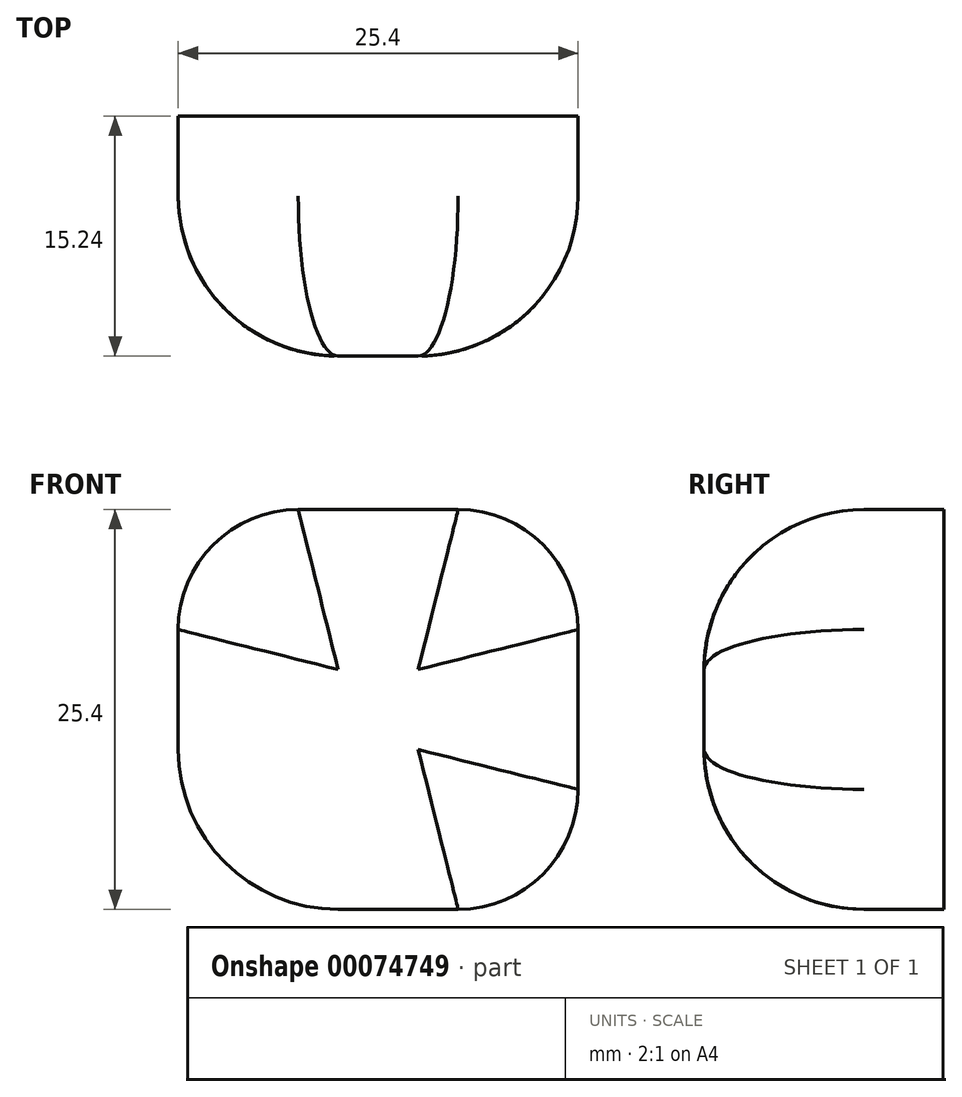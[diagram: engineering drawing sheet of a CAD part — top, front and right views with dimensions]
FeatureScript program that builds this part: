
annotation { "Feature Type Name" : "Feature", "Feature Type Description" : "" }
export const myFeature = defineFeature(function(context is Context, id is Id, definition is map)
    precondition{}
    {
        {
            var Q0;
            Q0=qCreatedBy(makeId("Front.planeOp"),FACE);
            var sketch = newSketch(context, id + "F0", { "sketchPlane" : qUnion([Q0])});
            skLineSegment(sketch, "E0", {"start": v(0, 0) * mm, "end": v(25.4, 0) * mm});
            skLineSegment(sketch, "E1", {"start": v(25.4, 0) * mm, "end": v(25.4, -25.4) * mm});
            skLineSegment(sketch, "E2", {"start": v(0, 0) * mm, "end": v(0, -25.4) * mm});
            skLineSegment(sketch, "E3", {"start": v(0, -25.4) * mm, "end": v(25.4, -25.4) * mm});
            skSolve(sketch);
        }
        {
            var Q0;
            Q0 = qSketchRegion(id + "F0", true);
            extrude(context, id + "F1", {"entities" : qUnion([Q0]), "depth" : 15.24 * mm});
        }
        {
            var Q0;
            Q0=makeQuery(id+"F1.opExtrude","SWEPT_EDGE",EDGE,{"disambiguationData":[OSD([sQuery(id+"F0.wireOp",EDGE,"E0"),sQuery(id+"F0.wireOp",EDGE,"E2")])]});
            fillet(context, id + "F2", {"entities" : qUnion([Q0]), "radius" : 7.62 * mm, "tangentPropagation" : true, "allowEdgeOverflow" : false});
        }
        {
            var Q0;
            Q0=makeQuery(id+"F1.opExtrude","SWEPT_EDGE",EDGE,{"disambiguationData":[OSD([sQuery(id+"F0.wireOp",EDGE,"E1"),sQuery(id+"F0.wireOp",EDGE,"E3")])]});
            fillet(context, id + "F3", {"entities" : qUnion([Q0]), "radius" : 7.62 * mm, "tangentPropagation" : true, "allowEdgeOverflow" : false});
        }
        {
            var Q0;
            Q0=makeQuery(id+"F1.opExtrude","SWEPT_EDGE",EDGE,{"disambiguationData":[OSD([sQuery(id+"F0.wireOp",EDGE,"E0"),sQuery(id+"F0.wireOp",EDGE,"E1")])]});
            fillet(context, id + "F4", {"entities" : qUnion([Q0]), "radius" : 7.62 * mm, "tangentPropagation" : true, "allowEdgeOverflow" : false});
        }
        {
            var Q0;
            Q0=makeQuery(id+"F1.opExtrude","SWEPT_EDGE",EDGE,{"disambiguationData":[OSD([sQuery(id+"F0.wireOp",EDGE,"E2"),sQuery(id+"F0.wireOp",EDGE,"E3")])]});
            fillet(context, id + "F5", {"entities" : qUnion([Q0]), "radius" : 10.16 * mm, "tangentPropagation" : true, "allowEdgeOverflow" : false});
        }
        {
            var Q0;
            Q0=makeQuery(id+"F1.opExtrude","CAP_EDGE",EDGE,{"disambiguationData":[OSD([sQuery(id+"F0.wireOp",EDGE,"E1")])],"isStart":false});
            fillet(context, id + "F6", {"entities" : qUnion([Q0]), "radius" : 10.16 * mm, "tangentPropagation" : true, "allowEdgeOverflow" : false});
        }
    });
